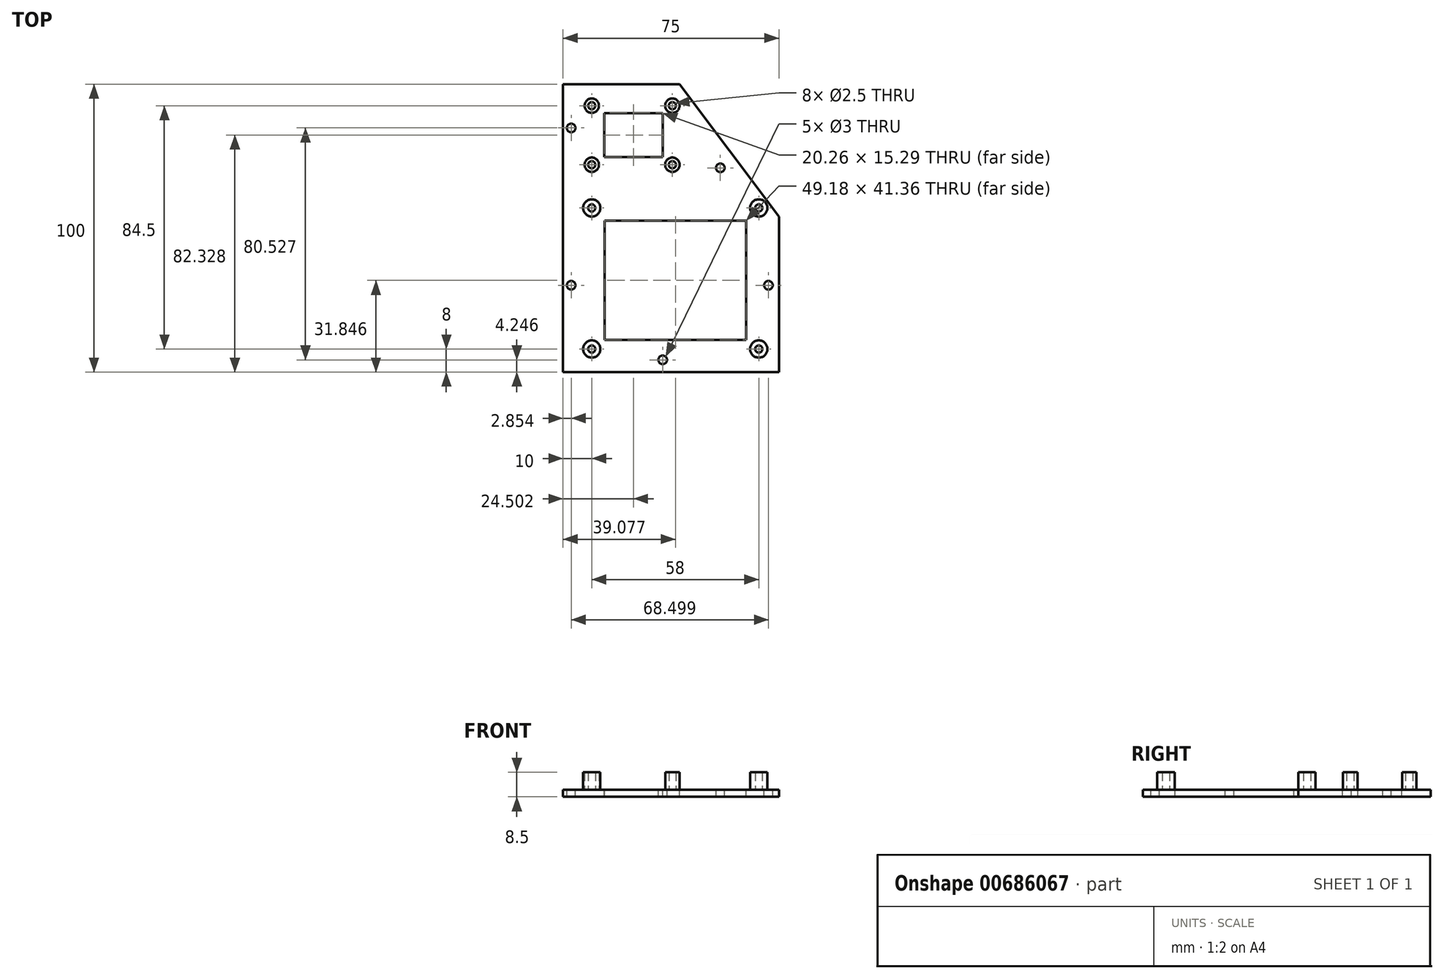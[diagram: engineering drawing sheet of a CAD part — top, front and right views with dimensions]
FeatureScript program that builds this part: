
annotation { "Feature Type Name" : "Feature", "Feature Type Description" : "" }
export const myFeature = defineFeature(function(context is Context, id is Id, definition is map)
    precondition{}
    {
        {
            var Q0;
            Q0=qCreatedBy(makeId("Top.planeOp"),FACE);
            var sketch = newSketch(context, id + "F0", { "sketchPlane" : qUnion([Q0])});
            skLineSegment(sketch, "E0.bottom", {"start": v(0, 0) * mm, "end": v(75, 0) * mm});
            skLineSegment(sketch, "E0.left", {"start": v(0, 0) * mm, "end": v(0, 100) * mm});
            skLineSegment(sketch, "E1", {"start": v(0, 100) * mm, "end": v(40.44, 100) * mm});
            skLineSegment(sketch, "E2", {"start": v(40.44, 100) * mm, "end": v(75, 53.95) * mm});
            skLineSegment(sketch, "E3", {"start": v(75, 53.95) * mm, "end": v(75, 0) * mm});
            skSolve(sketch);
        }
        {
            var Q0;
            Q0=qCreatedBy(makeId("Top.planeOp"),FACE);
            var sketch = newSketch(context, id + "F1", { "sketchPlane" : qUnion([Q0])});
            skLineSegment(sketch, "E4.bottom", {"start": v(10, 8) * mm, "end": v(68, 8) * mm, "construction": true});
            skLineSegment(sketch, "E4.top", {"start": v(10, 57) * mm, "end": v(68, 57) * mm, "construction": true});
            skLineSegment(sketch, "E4.left", {"start": v(10, 8) * mm, "end": v(10, 57) * mm, "construction": true});
            skLineSegment(sketch, "E4.right", {"start": v(68, 8) * mm, "end": v(68, 57) * mm, "construction": true});
            skLineSegment(sketch, "E5.bottom", {"start": v(10, 72) * mm, "end": v(38, 72) * mm, "construction": true});
            skLineSegment(sketch, "E5.top", {"start": v(10, 92.5) * mm, "end": v(38, 92.5) * mm, "construction": true});
            skLineSegment(sketch, "E5.left", {"start": v(10, 72) * mm, "end": v(10, 92.5) * mm, "construction": true});
            skLineSegment(sketch, "E5.right", {"start": v(38, 72) * mm, "end": v(38, 92.5) * mm, "construction": true});
            skCircle(sketch, "E6", {"center": v(10, 8) * mm, "radius": 3 * mm});
            skCircle(sketch, "E7", {"center": v(10, 8) * mm, "radius": 1.25 * mm});
            skCircle(sketch, "E8.0.1.0", {"center": v(10, 57) * mm, "radius": 3 * mm});
            skCircle(sketch, "E8.0.1.1", {"center": v(10, 57) * mm, "radius": 1.25 * mm});
            skCircle(sketch, "E8.1.0.0", {"center": v(68, 8) * mm, "radius": 3 * mm});
            skCircle(sketch, "E8.1.0.1", {"center": v(68, 8) * mm, "radius": 1.25 * mm});
            skCircle(sketch, "E8.1.1.0", {"center": v(68, 57) * mm, "radius": 3 * mm});
            skCircle(sketch, "E8.1.1.1", {"center": v(68, 57) * mm, "radius": 1.25 * mm});
            skCircle(sketch, "E9", {"center": v(10, 72) * mm, "radius": 2.5 * mm});
            skCircle(sketch, "E10", {"center": v(10, 72) * mm, "radius": 1.25 * mm});
            skCircle(sketch, "E11.0.1.0", {"center": v(10, 92.5) * mm, "radius": 2.5 * mm});
            skCircle(sketch, "E11.0.1.1", {"center": v(10, 92.5) * mm, "radius": 1.25 * mm});
            skCircle(sketch, "E11.1.0.0", {"center": v(38, 72) * mm, "radius": 2.5 * mm});
            skCircle(sketch, "E11.1.0.1", {"center": v(38, 72) * mm, "radius": 1.25 * mm});
            skCircle(sketch, "E11.1.1.0", {"center": v(38, 92.5) * mm, "radius": 2.5 * mm});
            skCircle(sketch, "E11.1.1.1", {"center": v(38, 92.5) * mm, "radius": 1.25 * mm});
            skSolve(sketch);
        }
        {
            var Q0;
            Q0 = qSketchRegion(id + "F1", true);
            extrude(context, id + "F2", {"entities" : qUnion([Q0]), "depth" : 6 * mm, "offsetDistance" : 25 * mm});
        }
        {
            var Q0;
            Q0=qCreatedBy(makeId("Top.planeOp"),FACE);
            var sketch = newSketch(context, id + "F3", { "sketchPlane" : qUnion([Q0])});
            skLineSegment(sketch, "E12.bottom", {"start": v(14.49, 52.52) * mm, "end": v(63.67, 52.52) * mm});
            skLineSegment(sketch, "E12.top", {"start": v(14.49, 11.17) * mm, "end": v(63.67, 11.17) * mm});
            skLineSegment(sketch, "E12.left", {"start": v(14.49, 52.52) * mm, "end": v(14.49, 11.17) * mm});
            skLineSegment(sketch, "E12.right", {"start": v(63.67, 52.52) * mm, "end": v(63.67, 11.17) * mm});
            skLineSegment(sketch, "E13.bottom", {"start": v(14.37, 89.97) * mm, "end": v(34.63, 89.97) * mm});
            skLineSegment(sketch, "E13.top", {"start": v(14.37, 74.68) * mm, "end": v(34.63, 74.68) * mm});
            skLineSegment(sketch, "E13.left", {"start": v(14.37, 89.97) * mm, "end": v(14.37, 74.68) * mm});
            skLineSegment(sketch, "E13.right", {"start": v(34.63, 89.97) * mm, "end": v(34.63, 74.68) * mm});
            skSolve(sketch);
        }
        {
            var Q0;
            Q0 = qSketchRegion(id + "F0", true);
            extrude(context, id + "F4", {"entities" : qUnion([Q0]), "oppositeDirection" : true, "depth" : 2.5 * mm, "offsetDistance" : 25 * mm});
        }
        {
            var Q0;
            Q0 = qSketchRegion(id + "F3", true);
            extrude(context, id + "F5", {"entities" : qUnion([Q0]), "operationType" : NewBodyOperationType.REMOVE, "oppositeDirection" : true, "depth" : 25 * mm, "offsetDistance" : 25 * mm});
        }
        {
            var Q0;
            Q0=makeQuery(id+"F4.opExtrude","CAP_FACE",FACE,{"disambiguationData":[OSD([sQuery(id+"F0.wireOp",EDGE,"E0.bottom"),sQuery(id+"F0.wireOp",EDGE,"E0.left"),sQuery(id+"F0.wireOp",EDGE,"E1"),sQuery(id+"F0.wireOp",EDGE,"E2"),sQuery(id+"F0.wireOp",EDGE,"E3")])],"isStart":true});
            var sketch = newSketch(context, id + "F6", { "sketchPlane" : qUnion([Q0])});
            skCircle(sketch, "E14", {"center": v(2.85, 84.77) * mm, "radius": 1.5 * mm});
            skCircle(sketch, "E15", {"center": v(2.85, 30.14) * mm, "radius": 1.5 * mm});
            skCircle(sketch, "E16", {"center": v(54.64, 70.9) * mm, "radius": 1.5 * mm});
            skCircle(sketch, "E17", {"center": v(71.35, 30.14) * mm, "radius": 1.5 * mm});
            skCircle(sketch, "E18", {"center": v(34.63, 4.25) * mm, "radius": 1.5 * mm});
            skSolve(sketch);
        }
        {
            var Q0;
            Q0 = qSketchRegion(id + "F6", true);
            extrude(context, id + "F7", {"entities" : qUnion([Q0]), "operationType" : NewBodyOperationType.REMOVE, "oppositeDirection" : true, "depth" : 25 * mm, "offsetDistance" : 25 * mm});
        }
    });
